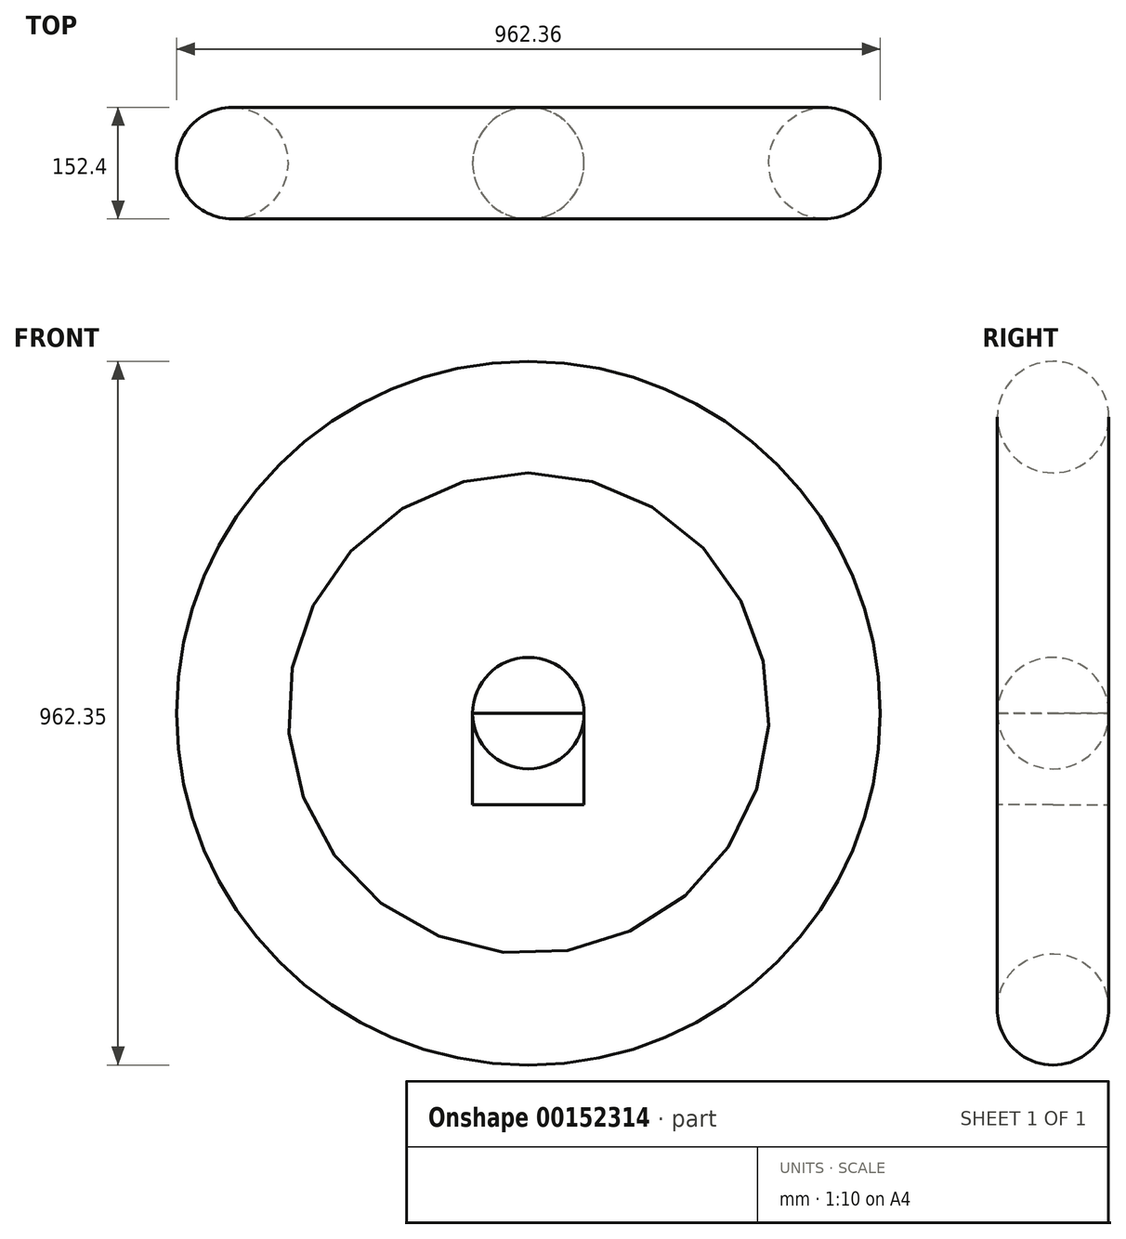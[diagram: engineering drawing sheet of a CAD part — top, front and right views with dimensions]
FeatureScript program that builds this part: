
annotation { "Feature Type Name" : "Feature", "Feature Type Description" : "" }
export const myFeature = defineFeature(function(context is Context, id is Id, definition is map)
    precondition{}
    {
        {
            var Q0;
            Q0=qCreatedBy(makeId("Right.planeOp"),FACE);
            var sketch = newSketch(context, id + "F0", { "sketchPlane" : qUnion([Q0])});
            skCircle(sketch, "E0", {"center": v(0, 529.88) * mm, "radius": 76.2 * mm});
            skArc(sketch, "E1", {"start": v(-76.2, 124.9) * mm, "mid": v(0, 48.7) * mm, "end": v(76.2, 124.9) * mm});
            skLineSegment(sketch, "E2", {"start": v(76.2, 124.9) * mm, "end": v(-76.2, 124.9) * mm});
            skSolve(sketch);
        }
        {
            var Q0;
            Q0 = qSketchRegion(id + "F0", true);
            var Q1;
            Q1=sQuery(id+"F0.wireOp",EDGE,"E2");
            revolve(context, id + "F1", {"entities" : qUnion([Q0]), "axis" : qUnion([Q1]), "revolveType" : RevolveType.FULL});
        }
        {
            var Q0;
            Q0=qCreatedBy(makeId("Top.planeOp"),FACE);
            var sketch = newSketch(context, id + "F2", { "sketchPlane" : qUnion([Q0])});
            skCircle(sketch, "E3", {"center": v(0, 0) * mm, "radius": 76.2 * mm});
            skSolve(sketch);
        }
        {
            var Q0;
            Q0 = qSketchRegion(id + "F2", true);
            extrude(context, id + "F3", {"entities" : qUnion([Q0]), "endBound" : BoundingType.UP_TO_NEXT, "depth" : 304.8 * mm});
        }
    });
